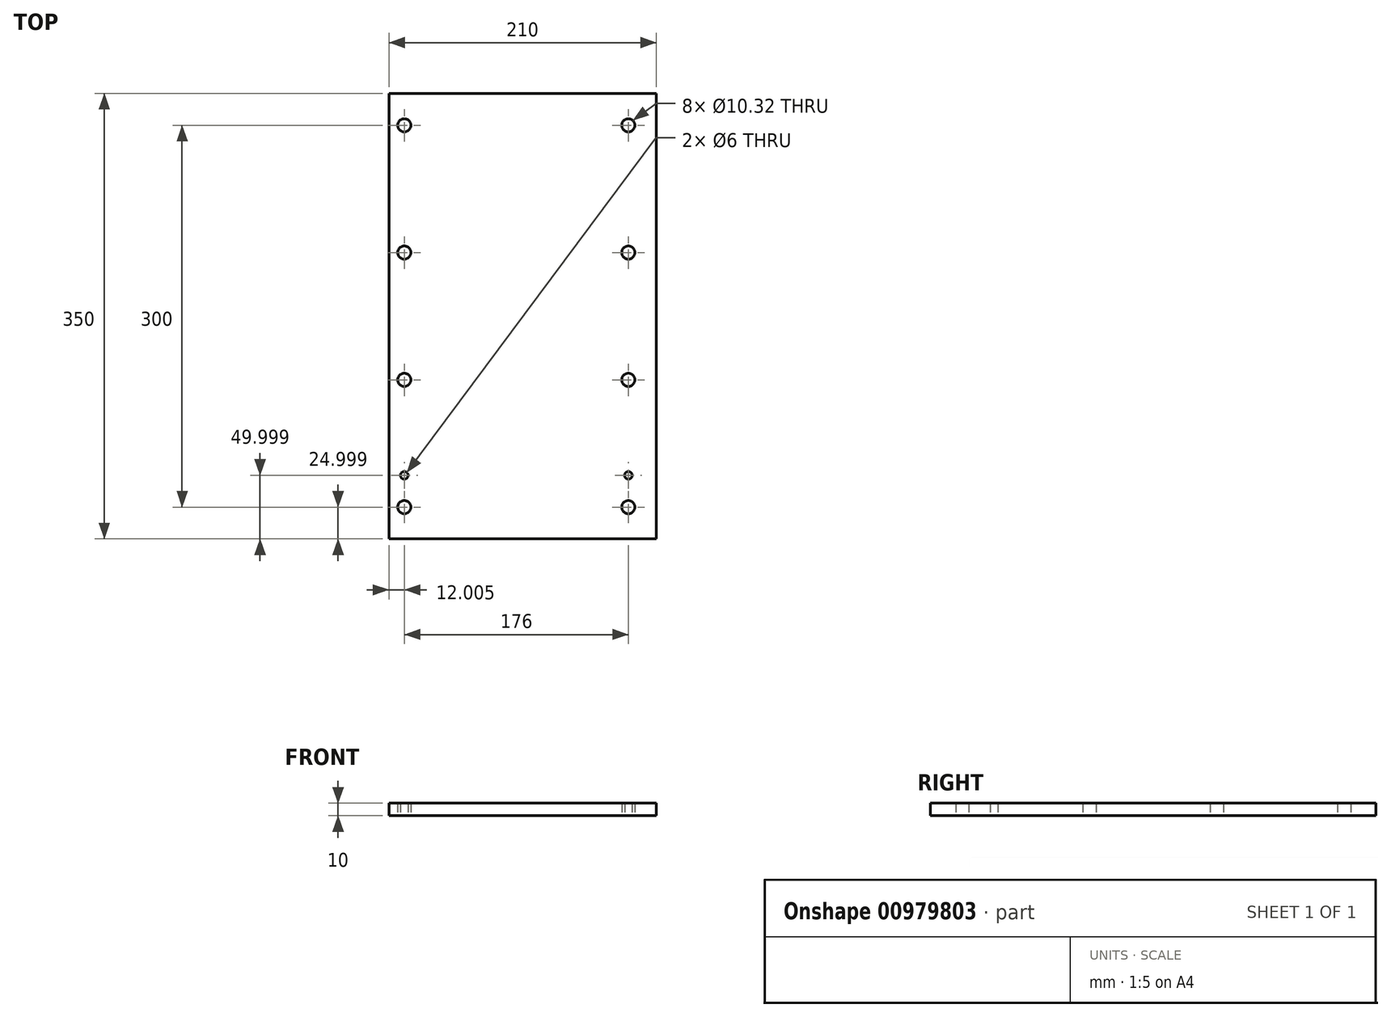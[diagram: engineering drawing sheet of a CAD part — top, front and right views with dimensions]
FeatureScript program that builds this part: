
annotation { "Feature Type Name" : "Feature", "Feature Type Description" : "" }
export const myFeature = defineFeature(function(context is Context, id is Id, definition is map)
    precondition{}
    {
        {
            var Q0;
            Q0=qCreatedBy(makeId("Top.planeOp"),FACE);
            var sketch = newSketch(context, id + "F0", { "sketchPlane" : qUnion([Q0])});
            skLineSegment(sketch, "E0.bottom", {"start": v(-110.24, 186.62) * mm, "end": v(99.76, 186.62) * mm});
            skLineSegment(sketch, "E0.top", {"start": v(-110.24, -163.38) * mm, "end": v(99.76, -163.38) * mm});
            skLineSegment(sketch, "E0.left", {"start": v(-110.24, 186.62) * mm, "end": v(-110.24, -163.38) * mm});
            skLineSegment(sketch, "E0.right", {"start": v(99.76, 186.62) * mm, "end": v(99.76, -163.38) * mm});
            skPoint(sketch, "E1", {"position": v(-98.24, -138.38) * mm});
            skPoint(sketch, "E2", {"position": v(-98.24, -113.38) * mm});
            skPoint(sketch, "E3", {"position": v(-98.24, 61.62) * mm});
            skPoint(sketch, "E4", {"position": v(-98.24, 161.62) * mm});
            skPoint(sketch, "E5", {"position": v(-98.24, -38.38) * mm});
            skPoint(sketch, "E6", {"position": v(77.76, 161.62) * mm});
            skPoint(sketch, "E7", {"position": v(77.76, 61.62) * mm});
            skPoint(sketch, "E8", {"position": v(77.76, -38.38) * mm});
            skPoint(sketch, "E9", {"position": v(77.76, -113.38) * mm});
            skPoint(sketch, "E10", {"position": v(77.76, -138.38) * mm});
            skCircle(sketch, "E11", {"center": v(-98.24, 161.62) * mm, "radius": 5.16 * mm});
            skCircle(sketch, "E12", {"center": v(-98.24, 61.62) * mm, "radius": 5.16 * mm});
            skCircle(sketch, "E13", {"center": v(-98.24, -38.38) * mm, "radius": 5.16 * mm});
            skCircle(sketch, "E14", {"center": v(-98.24, -113.38) * mm, "radius": 3 * mm});
            skCircle(sketch, "E15", {"center": v(-98.24, -138.38) * mm, "radius": 5.16 * mm});
            skCircle(sketch, "E16", {"center": v(77.76, 161.62) * mm, "radius": 5.16 * mm});
            skCircle(sketch, "E17", {"center": v(77.76, 61.62) * mm, "radius": 5.16 * mm});
            skCircle(sketch, "E18", {"center": v(77.76, -38.38) * mm, "radius": 5.16 * mm});
            skCircle(sketch, "E19", {"center": v(77.76, -113.38) * mm, "radius": 3 * mm});
            skCircle(sketch, "E20", {"center": v(77.76, -138.38) * mm, "radius": 5.16 * mm});
            skSolve(sketch);
        }
        {
            var Q0;
            Q0 = qSketchRegion(id + "F0", true);
            extrude(context, id + "F1", {"entities" : qUnion([Q0]), "depth" : 10 * mm, "offsetDistance" : 25 * mm});
        }
    });
